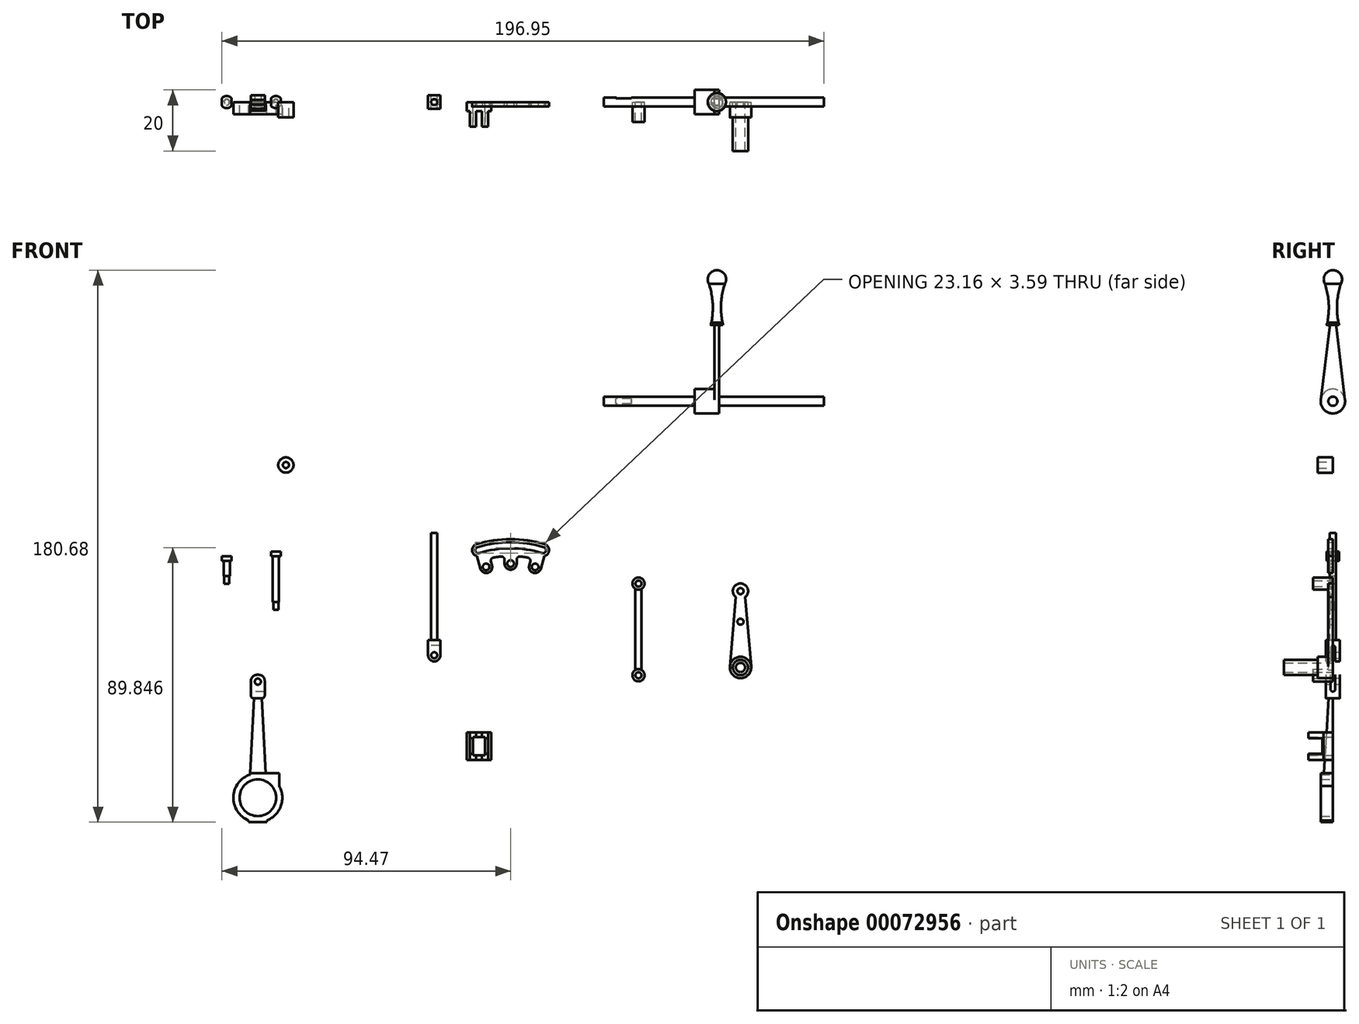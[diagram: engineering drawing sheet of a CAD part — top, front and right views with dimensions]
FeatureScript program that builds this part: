
annotation { "Feature Type Name" : "Feature", "Feature Type Description" : "" }
export const myFeature = defineFeature(function(context is Context, id is Id, definition is map)
    precondition{}
    {
        {
            var Q0;
            Q0=qCreatedBy(makeId("Front.planeOp"),FACE);
            var sketch = newSketch(context, id + "F0", { "sketchPlane" : qUnion([Q0])});
            skLineSegment(sketch, "E0", {"start": v(0, 0) * mm, "end": v(0, 28) * mm});
            skLineSegment(sketch, "E1", {"start": v(0, 0) * mm, "end": v(-7.48, 26.98) * mm});
            skCircle(sketch, "E2", {"center": v(0, 30) * mm, "radius": 1.1 * mm});
            skCircle(sketch, "E3", {"center": v(-8.02, 28.9) * mm, "radius": 1.1 * mm});
            skLineSegment(sketch, "E4", {"start": v(0, 0) * mm, "end": v(8.28, 26.93) * mm});
            skArc(sketch, "E5", {"start": v(11.08, 32.47) * mm, "mid": v(12.58, 34.36) * mm, "end": v(11.17, 36.32) * mm});
            skArc(sketch, "E6", {"start": v(10.3, 33.45) * mm, "mid": v(11.54, 34.11) * mm, "end": v(10.88, 35.36) * mm});
            skArc(sketch, "E7", {"start": v(-9.94, 28.37) * mm, "mid": v(-7.48, 26.98) * mm, "end": v(-6.09, 29.44) * mm});
            skLineSegment(sketch, "E8", {"start": v(-6.09, 29.44) * mm, "end": v(-6.44, 30.7) * mm});
            skLineSegment(sketch, "E9", {"start": v(-9.94, 28.37) * mm, "end": v(-10.73, 31.2) * mm});
            skArc(sketch, "E10.trimOffspring", {"start": v(9.93, 28.31) * mm, "mid": v(8.02, 28.9) * mm, "end": v(6.07, 29.38) * mm});
            skArc(sketch, "E11", {"start": v(10.3, 33.45) * mm, "mid": v(0, 35) * mm, "end": v(-10.3, 33.45) * mm});
            skArc(sketch, "E12", {"start": v(10.88, 35.36) * mm, "mid": v(0, 37) * mm, "end": v(-10.88, 35.36) * mm});
            skArc(sketch, "E13.MirrorC", {"start": v(-10.3, 33.45) * mm, "mid": v(-11.54, 34.11) * mm, "end": v(-10.88, 35.36) * mm});
            skArc(sketch, "E14.MirrorC", {"start": v(-11.08, 32.47) * mm, "mid": v(-12.58, 34.36) * mm, "end": v(-11.17, 36.32) * mm});
            skArc(sketch, "E15", {"start": v(11.17, 36.32) * mm, "mid": v(0, 38) * mm, "end": v(-11.17, 36.32) * mm});
            skLineSegment(sketch, "E16", {"start": v(-10.73, 31.2) * mm, "end": v(-11.08, 32.47) * mm});
            skLineSegment(sketch, "E17.MirrorCS", {"start": v(10.73, 31.2) * mm, "end": v(11.08, 32.47) * mm});
            skLineSegment(sketch, "E18.MirrorCS", {"start": v(9.94, 28.37) * mm, "end": v(10.73, 31.2) * mm});
            skLineSegment(sketch, "E19.MirrorCS", {"start": v(6.09, 29.44) * mm, "end": v(6.44, 30.7) * mm});
            skCircle(sketch, "E20.MirrorC", {"center": v(8.02, 28.9) * mm, "radius": 1.1 * mm});
            skArc(sketch, "E21.MirrorCS", {"start": v(9.94, 28.37) * mm, "mid": v(7.48, 26.98) * mm, "end": v(6.09, 29.44) * mm});
            skArc(sketch, "E22", {"start": v(-2, 30) * mm, "mid": v(0, 28) * mm, "end": v(2, 30) * mm});
            skLineSegment(sketch, "E23", {"start": v(0, 30) * mm, "end": v(2, 30) * mm});
            skLineSegment(sketch, "E24", {"start": v(2, 30) * mm, "end": v(2, 31.3) * mm});
            skLineSegment(sketch, "E25.MirrorCS", {"start": v(-2, 30) * mm, "end": v(-2, 31.3) * mm});
            skArc(sketch, "E26.trimOffspring", {"start": v(5.65, 31.95) * mm, "mid": v(4.38, 32.15) * mm, "end": v(3.1, 32.3) * mm});
            skArc(sketch, "E27.trimOffspring", {"start": v(-3.1, 32.3) * mm, "mid": v(-4.38, 32.15) * mm, "end": v(-5.65, 31.95) * mm});
            skPoint(sketch, "E28.trimOffspring.end.orphan", {"position": v(10, 32.5) * mm});
            skPoint(sketch, "E29.visualSharp", {"position": v(-6.73, 31.74) * mm});
            skArc(sketch, "E29.filletArc", {"start": v(-5.65, 31.95) * mm, "mid": v(-6.32, 31.5) * mm, "end": v(-6.44, 30.7) * mm});
            skPoint(sketch, "E30.visualSharp", {"position": v(-2, 32.39) * mm});
            skArc(sketch, "E30.filletArc", {"start": v(-2, 31.3) * mm, "mid": v(-2.33, 32.05) * mm, "end": v(-3.1, 32.3) * mm});
            skPoint(sketch, "E31.visualSharp", {"position": v(2, 32.39) * mm});
            skArc(sketch, "E31.filletArc", {"start": v(3.1, 32.3) * mm, "mid": v(2.33, 32.05) * mm, "end": v(2, 31.3) * mm});
            skPoint(sketch, "E32.visualSharp", {"position": v(6.73, 31.74) * mm});
            skArc(sketch, "E32.filletArc", {"start": v(6.44, 30.7) * mm, "mid": v(6.32, 31.5) * mm, "end": v(5.65, 31.95) * mm});
            skSolve(sketch);
        }
        {
            var Q0;
            Q0=makeQuery(id+"F0.imprint","IMPRINT",FACE,{"disambiguationData":[TD([[makeQuery(id+"F0.imprint","IMPRINT",EDGE,{"derivedFrom":sQuery(id+"F0.wireOp",EDGE,"E2")}),-1.0]])]});
            var Q1;
            {var subQ0=sQuery(id+"F0.wireOp",EDGE,"E21.MirrorCS");var subQ1=sQuery(id+"F0.wireOp",EDGE,"E10.trimOffspring");var subQ7=makeQuery(id+"F0.imprint","INTERSECT",VERTEX,{"disambiguationData":[OD(0.0)],"derivedFrom":[subQ1,subQ0]});Q1=makeQuery(id+"F0.imprint","IMPRINT",FACE,{"disambiguationData":[TD([[makeQuery(id+"F0.imprint","IMPRINT",EDGE,{"disambiguationData":[TD([[subQ7,-1.0]])],"derivedFrom":subQ1}),1.0]])]});}
            extrude(context, id + "F1", {"entities" : qUnion([Q0, Q1]), "depth" : 1.5 * mm});
        }
        {
            var Q0;
            Q0=qCreatedBy(makeId("Front.planeOp"),FACE);
            var sketch = newSketch(context, id + "F2", { "sketchPlane" : qUnion([Q0])});
            skLineSegment(sketch, "E33", {"start": v(0, 0) * mm, "end": v(-25, 0) * mm});
            skCircle(sketch, "E34", {"center": v(-25, 0) * mm, "radius": 1 * mm});
            skArc(sketch, "E35", {"start": v(-27, 0) * mm, "mid": v(-25, -2) * mm, "end": v(-23, 0) * mm});
            skLineSegment(sketch, "E36", {"start": v(-27, 0) * mm, "end": v(-27, 5) * mm});
            skLineSegment(sketch, "E37", {"start": v(-25, 0) * mm, "end": v(-25, -0.62) * mm});
            skLineSegment(sketch, "E38.MirrorCS", {"start": v(-23, 0) * mm, "end": v(-23, 5) * mm});
            skLineSegment(sketch, "E39", {"start": v(-27, 5) * mm, "end": v(-23, 5) * mm});
            skSolve(sketch);
        }
        {
            var Q0;
            Q0 = qSketchRegion(id + "F2", true);
            extrude(context, id + "F3", {"entities" : qUnion([Q0]), "endBound" : BoundingType.SYMMETRIC, "depth" : 4.5 * mm});
        }
        {
            var Q0;
            Q0=makeQuery(id+"F3.opExtrude","SWEPT_FACE",FACE,{"disambiguationData":[OSD([sQuery(id+"F2.wireOp",EDGE,"E36")])]});
            var sketch = newSketch(context, id + "F4", { "sketchPlane" : qUnion([Q0])});
            skLineSegment(sketch, "E40", {"start": v(0, 0) * mm, "end": v(0, 2.5) * mm});
            skPoint(sketch, "E40.endSnap0", {"position": v(0, 0) * mm});
            skArc(sketch, "E41", {"start": v(0.75, 2.5) * mm, "mid": v(0, 3.25) * mm, "end": v(-0.75, 2.5) * mm});
            skLineSegment(sketch, "E42", {"start": v(-0.75, 2.5) * mm, "end": v(-0.75, -3.17) * mm});
            skLineSegment(sketch, "E43", {"start": v(-0.75, -3.17) * mm, "end": v(0, -3.17) * mm});
            skLineSegment(sketch, "E44", {"start": v(0, -3.17) * mm, "end": v(1.6, -3.17) * mm});
            skLineSegment(sketch, "E45", {"start": v(0.75, 2.5) * mm, "end": v(0.75, -3.17) * mm});
            skSolve(sketch);
        }
        {
            var Q0;
            Q0 = qSketchRegion(id + "F4", true);
            extrude(context, id + "F5", {"entities" : qUnion([Q0]), "operationType" : NewBodyOperationType.REMOVE, "endBound" : BoundingType.SYMMETRIC, "oppositeDirection" : true, "depth" : 25 * mm});
        }
        {
            var Q0;
            Q0=makeQuery(id+"F3.opExtrude","SWEPT_FACE",FACE,{"disambiguationData":[OSD([sQuery(id+"F2.wireOp",EDGE,"E39")])]});
            var sketch = newSketch(context, id + "F6", { "sketchPlane" : qUnion([Q0])});
            skCircle(sketch, "E46", {"center": v(-25, 0) * mm, "radius": 1 * mm});
            skPoint(sketch, "E46.centerSnap0", {"position": v(-25, 2.25) * mm});
            skPoint(sketch, "E46.centerSnap1", {"position": v(-27, 0) * mm});
            skSolve(sketch);
        }
        {
            var Q0;
            Q0 = qSketchRegion(id + "F6", true);
            extrude(context, id + "F7", {"entities" : qUnion([Q0]), "operationType" : NewBodyOperationType.ADD, "depth" : 35 * mm});
        }
        {
            var Q0;
            Q0=qCreatedBy(makeId("Front.planeOp"),FACE);
            var sketch = newSketch(context, id + "F8", { "sketchPlane" : qUnion([Q0])});
            skCircle(sketch, "E47", {"center": v(41.83, 23.44) * mm, "radius": 1 * mm});
            skCircle(sketch, "E48", {"center": v(41.83, 23.44) * mm, "radius": 2 * mm});
            skCircle(sketch, "E49", {"center": v(41.83, -6.56) * mm, "radius": 1 * mm});
            skCircle(sketch, "E50", {"center": v(41.83, -6.56) * mm, "radius": 2 * mm});
            skLineSegment(sketch, "E51", {"start": v(41.83, 23.44) * mm, "end": v(40.83, 23.44) * mm});
            skLineSegment(sketch, "E52", {"start": v(40.83, 21.7) * mm, "end": v(40.83, -4.83) * mm});
            skLineSegment(sketch, "E53.MirrorCS", {"start": v(42.83, 21.7) * mm, "end": v(42.83, -4.83) * mm});
            skSolve(sketch);
        }
        {
            var Q0;
            {var subQ0=sQuery(id+"F8.wireOp",EDGE,"E52");Q0=makeQuery(id+"F8.imprint","IMPRINT",FACE,{"disambiguationData":[TD([[makeQuery(id+"F8.imprint","IMPRINT",EDGE,{"derivedFrom":subQ0}),1.0]])]});}
            extrude(context, id + "F9", {"entities" : qUnion([Q0]), "depth" : 1.5 * mm});
        }
        {
            var Q0;
            Q0=makeQuery(id+"F8.imprint","IMPRINT",FACE,{"disambiguationData":[TD([[makeQuery(id+"F8.imprint","IMPRINT",EDGE,{"derivedFrom":sQuery(id+"F8.wireOp",EDGE,"E49")}),-1.0]])]});
            var Q1;
            Q1=makeQuery(id+"F8.imprint","IMPRINT",FACE,{"disambiguationData":[TD([[makeQuery(id+"F8.imprint","IMPRINT",EDGE,{"derivedFrom":sQuery(id+"F8.wireOp",EDGE,"E47")}),-1.0]])]});
            extrude(context, id + "F10", {"entities" : qUnion([Q0, Q1]), "operationType" : NewBodyOperationType.ADD, "depth" : 6.5 * mm});
        }
        {
            var Q0;
            Q0=qCreatedBy(makeId("Front.planeOp"),FACE);
            var sketch = newSketch(context, id + "F11", { "sketchPlane" : qUnion([Q0])});
            skLineSegment(sketch, "E54", {"start": v(75.2, -4.01) * mm, "end": v(75.2, 20.99) * mm});
            skCircle(sketch, "E55", {"center": v(75.2, 20.99) * mm, "radius": 1 * mm});
            skCircle(sketch, "E56", {"center": v(75.2, 20.99) * mm, "radius": 2.5 * mm});
            skCircle(sketch, "E57", {"center": v(75.2, -4.01) * mm, "radius": 2.5 * mm});
            skCircle(sketch, "E58", {"center": v(75.2, -4.01) * mm, "radius": 3.5 * mm});
            skCircle(sketch, "E59", {"center": v(75.2, -4.01) * mm, "radius": 1.5 * mm});
            skLineSegment(sketch, "E60", {"start": v(76.74, 19.02) * mm, "end": v(78.68, -3.71) * mm});
            skLineSegment(sketch, "E61.MirrorCS", {"start": v(73.65, 19.02) * mm, "end": v(71.7, -3.71) * mm});
            skLineSegment(sketch, "E62", {"start": v(75.2, 20.99) * mm, "end": v(75.2, 10.99) * mm});
            skCircle(sketch, "E63", {"center": v(75.2, 10.99) * mm, "radius": 1 * mm});
            skSolve(sketch);
        }
        {
            var Q0;
            {var subQ0=sQuery(id+"F11.wireOp",EDGE,"E60");Q0=makeQuery(id+"F11.imprint","IMPRINT",FACE,{"disambiguationData":[TD([[makeQuery(id+"F11.imprint","IMPRINT",EDGE,{"derivedFrom":subQ0}),-1.0]])]});}
            var Q1;
            {var subQ0=sQuery(id+"F11.wireOp",EDGE,"E61.MirrorCS");Q1=makeQuery(id+"F11.imprint","IMPRINT",FACE,{"disambiguationData":[TD([[makeQuery(id+"F11.imprint","IMPRINT",EDGE,{"derivedFrom":subQ0}),1.0]])]});}
            var Q2;
            Q2=makeQuery(id+"F11.imprint","IMPRINT",FACE,{"disambiguationData":[TD([[makeQuery(id+"F11.imprint","IMPRINT",EDGE,{"derivedFrom":sQuery(id+"F11.wireOp",EDGE,"E55")}),-1.0]])]});
            extrude(context, id + "F12", {"entities" : qUnion([Q0, Q1, Q2]), "depth" : 1.5 * mm});
        }
        {
            var Q0;
            Q0=makeQuery(id+"F11.imprint","IMPRINT",FACE,{"disambiguationData":[TD([[makeQuery(id+"F11.imprint","IMPRINT",EDGE,{"derivedFrom":sQuery(id+"F11.wireOp",EDGE,"E57")}),-1.0]])]});
            extrude(context, id + "F13", {"entities" : qUnion([Q0]), "operationType" : NewBodyOperationType.ADD, "depth" : 5 * mm});
        }
        {
            var Q0;
            Q0=makeQuery(id+"F11.imprint","IMPRINT",FACE,{"disambiguationData":[TD([[makeQuery(id+"F11.imprint","IMPRINT",EDGE,{"derivedFrom":sQuery(id+"F11.wireOp",EDGE,"E57")}),1.0]])]});
            extrude(context, id + "F14", {"entities" : qUnion([Q0]), "operationType" : NewBodyOperationType.ADD, "depth" : 16 * mm});
        }
        {
            var Q0;
            Q0=qCreatedBy(makeId("Front.planeOp"),FACE);
            var sketch = newSketch(context, id + "F15", { "sketchPlane" : qUnion([Q0])});
            skLineSegment(sketch, "E64.left", {"start": v(-14.34, -25.22) * mm, "end": v(-14.34, -29.72) * mm});
            skLineSegment(sketch, "E65", {"start": v(-14.34, -25.22) * mm, "end": v(-10.34, -25.22) * mm});
            skLineSegment(sketch, "E66", {"start": v(-10.34, -25.22) * mm, "end": v(-10.34, -26.72) * mm});
            skLineSegment(sketch, "E67.MirrorCS", {"start": v(-6.34, -25.22) * mm, "end": v(-10.34, -25.22) * mm});
            skLineSegment(sketch, "E68", {"start": v(-14.34, -29.72) * mm, "end": v(-15.04, -29.72) * mm});
            skLineSegment(sketch, "E69.MirrorCS", {"start": v(-14.34, -34.22) * mm, "end": v(-14.34, -29.72) * mm});
            skLineSegment(sketch, "E70", {"start": v(-10.34, -26.72) * mm, "end": v(-12.34, -26.72) * mm});
            skLineSegment(sketch, "E71.MirrorCS", {"start": v(-10.34, -32.72) * mm, "end": v(-12.34, -32.72) * mm});
            skLineSegment(sketch, "E72.MirrorCS", {"start": v(-10.34, -26.72) * mm, "end": v(-8.34, -26.72) * mm});
            skLineSegment(sketch, "E73.MirrorCS", {"start": v(-10.34, -32.72) * mm, "end": v(-8.34, -32.72) * mm});
            skLineSegment(sketch, "E74", {"start": v(-12.34, -26.72) * mm, "end": v(-12.34, -32.72) * mm});
            skLineSegment(sketch, "E75", {"start": v(-8.34, -26.72) * mm, "end": v(-8.34, -32.87) * mm});
            skLineSegment(sketch, "E76.MirrorCS", {"start": v(-6.34, -25.22) * mm, "end": v(-6.34, -29.72) * mm});
            skLineSegment(sketch, "E77.MirrorCS", {"start": v(-6.34, -34.22) * mm, "end": v(-6.34, -29.72) * mm});
            skLineSegment(sketch, "E78.MirrorCS", {"start": v(-14.34, -34.22) * mm, "end": v(-10.34, -34.22) * mm});
            skLineSegment(sketch, "E79.MirrorCS", {"start": v(-6.34, -34.22) * mm, "end": v(-10.34, -34.22) * mm});
            skSolve(sketch);
        }
        {
            var Q0;
            Q0 = qSketchRegion(id + "F15", true);
            extrude(context, id + "F16", {"entities" : qUnion([Q0]), "depth" : 8 * mm});
        }
        {
            var Q0;
            Q0=makeQuery(id+"F16.opExtrude","SWEPT_FACE",FACE,{"disambiguationData":[OSD([sQuery(id+"F15.wireOp",EDGE,"E76.MirrorCS"),sQuery(id+"F15.wireOp",EDGE,"E77.MirrorCS")])]});
            var sketch = newSketch(context, id + "F17", { "sketchPlane" : qUnion([Q0])});
            skLineSegment(sketch, "E80", {"start": v(0, -29.72) * mm, "end": v(0, -27.22) * mm});
            skLineSegment(sketch, "E81", {"start": v(0, -27.22) * mm, "end": v(-3.5, -27.22) * mm});
            skLineSegment(sketch, "E82", {"start": v(-3.5, -27.22) * mm, "end": v(-3.5, -29.72) * mm});
            skLineSegment(sketch, "E83", {"start": v(0, -29.72) * mm, "end": v(2.8, -29.72) * mm});
            skLineSegment(sketch, "E84.MirrorCS", {"start": v(-3.5, -32.22) * mm, "end": v(-3.5, -29.72) * mm});
            skLineSegment(sketch, "E85.MirrorCS", {"start": v(0, -32.22) * mm, "end": v(-3.5, -32.22) * mm});
            skLineSegment(sketch, "E86", {"start": v(-3.5, -32.22) * mm, "end": v(-8, -32.22) * mm});
            skLineSegment(sketch, "E87", {"start": v(-8, -32.22) * mm, "end": v(-8, -34.22) * mm});
            skLineSegment(sketch, "E88", {"start": v(-8, -34.22) * mm, "end": v(0, -34.22) * mm});
            skLineSegment(sketch, "E89", {"start": v(0, -34.22) * mm, "end": v(0, -32.22) * mm});
            skLineSegment(sketch, "E90.MirrorCS", {"start": v(-3.5, -27.22) * mm, "end": v(-8, -27.22) * mm});
            skLineSegment(sketch, "E91.MirrorCS", {"start": v(-8, -27.22) * mm, "end": v(-8, -25.22) * mm});
            skLineSegment(sketch, "E92.MirrorCS", {"start": v(-8, -25.22) * mm, "end": v(0, -25.22) * mm});
            skLineSegment(sketch, "E93.MirrorCS", {"start": v(0, -25.22) * mm, "end": v(0, -27.22) * mm});
            skLineSegment(sketch, "E94", {"start": v(-8, -32.22) * mm, "end": v(-8, -27.22) * mm});
            skSolve(sketch);
        }
        {
            var Q0;
            Q0=makeQuery(id+"F17.imprint","IMPRINT",FACE,{"disambiguationData":[TD([[makeQuery(id+"F17.imprint","IMPRINT",EDGE,{"derivedFrom":sQuery(id+"F17.wireOp",EDGE,"E82")}),-1.0]])]});
            extrude(context, id + "F18", {"entities" : qUnion([Q0]), "operationType" : NewBodyOperationType.REMOVE, "oppositeDirection" : true, "depth" : 25 * mm});
        }
        {
            var Q0;
            Q0=makeQuery(id+"F16.opExtrude","SWEPT_FACE",FACE,{"disambiguationData":[OSD([sQuery(id+"F15.wireOp",EDGE,"E78.MirrorCS"),sQuery(id+"F15.wireOp",EDGE,"E79.MirrorCS")])]});
            var sketch = newSketch(context, id + "F19", { "sketchPlane" : qUnion([Q0])});
            skLineSegment(sketch, "E95", {"start": v(-14.34, 0) * mm, "end": v(-14.34, 3) * mm});
            skLineSegment(sketch, "E96", {"start": v(-10.34, 0) * mm, "end": v(-10.34, 8) * mm});
            skLineSegment(sketch, "E97", {"start": v(-10.34, 8) * mm, "end": v(-11.34, 8) * mm});
            skLineSegment(sketch, "E98", {"start": v(-11.34, 8) * mm, "end": v(-13.34, 8) * mm});
            skLineSegment(sketch, "E99", {"start": v(-14.34, 3) * mm, "end": v(-13.34, 3) * mm});
            skLineSegment(sketch, "E100", {"start": v(-13.34, 3) * mm, "end": v(-13.34, 8) * mm});
            skLineSegment(sketch, "E101", {"start": v(-13.34, 8) * mm, "end": v(-11.34, 8) * mm});
            skLineSegment(sketch, "E102", {"start": v(-11.34, 8) * mm, "end": v(-11.34, 3) * mm});
            skLineSegment(sketch, "E103", {"start": v(-11.34, 3) * mm, "end": v(-10.34, 3) * mm});
            skLineSegment(sketch, "E104.MirrorCS", {"start": v(-9.34, 3) * mm, "end": v(-10.34, 3) * mm});
            skLineSegment(sketch, "E105.MirrorCS", {"start": v(-9.34, 8) * mm, "end": v(-9.34, 3) * mm});
            skLineSegment(sketch, "E106.MirrorCS", {"start": v(-7.34, 8) * mm, "end": v(-9.34, 8) * mm});
            skLineSegment(sketch, "E107.MirrorCS", {"start": v(-7.34, 3) * mm, "end": v(-7.34, 8) * mm});
            skLineSegment(sketch, "E108.MirrorCS", {"start": v(-6.34, 3) * mm, "end": v(-7.34, 3) * mm});
            skLineSegment(sketch, "E109.MirrorCS", {"start": v(-6.34, 0) * mm, "end": v(-6.34, 3) * mm});
            skLineSegment(sketch, "E110.bottom", {"start": v(-14.34, 3) * mm, "end": v(-6.34, 3) * mm});
            skLineSegment(sketch, "E110.top", {"start": v(-14.34, 8) * mm, "end": v(-6.34, 8) * mm});
            skLineSegment(sketch, "E110.left", {"start": v(-14.34, 3) * mm, "end": v(-14.34, 8) * mm});
            skLineSegment(sketch, "E110.right", {"start": v(-6.34, 3) * mm, "end": v(-6.34, 8) * mm});
            skSolve(sketch);
        }
        {
            var Q0;
            {var subQ0=sQuery(id+"F19.wireOp",EDGE,"E100");Q0=makeQuery(id+"F19.imprint","IMPRINT",FACE,{"disambiguationData":[TD([[makeQuery(id+"F19.imprint","IMPRINT",EDGE,{"derivedFrom":subQ0}),1.0]])]});}
            var Q1;
            {var subQ5=sQuery(id+"F19.wireOp",EDGE,"E102");Q1=makeQuery(id+"F19.imprint","IMPRINT",FACE,{"disambiguationData":[TD([[makeQuery(id+"F19.imprint","IMPRINT",EDGE,{"derivedFrom":subQ5}),1.0]])]});}
            var Q2;
            {var subQ5=sQuery(id+"F19.wireOp",EDGE,"E105.MirrorCS");Q2=makeQuery(id+"F19.imprint","IMPRINT",FACE,{"disambiguationData":[TD([[makeQuery(id+"F19.imprint","IMPRINT",EDGE,{"derivedFrom":subQ5}),-1.0]])]});}
            var Q3;
            {var subQ0=sQuery(id+"F19.wireOp",EDGE,"E107.MirrorCS");Q3=makeQuery(id+"F19.imprint","IMPRINT",FACE,{"disambiguationData":[TD([[makeQuery(id+"F19.imprint","IMPRINT",EDGE,{"derivedFrom":subQ0}),-1.0]])]});}
            extrude(context, id + "F20", {"entities" : qUnion([Q0, Q1, Q2, Q3]), "operationType" : NewBodyOperationType.REMOVE, "oppositeDirection" : true, "depth" : 25 * mm});
        }
        {
            var Q0;
            Q0=qCreatedBy(makeId("Front.planeOp"),FACE);
            var sketch = newSketch(context, id + "F21", { "sketchPlane" : qUnion([Q0])});
            skCircle(sketch, "E111", {"center": v(-82.7, -46.64) * mm, "radius": 8 * mm});
            skCircle(sketch, "E112", {"center": v(-82.7, -46.64) * mm, "radius": 6 * mm});
            skLineSegment(sketch, "E113", {"start": v(-82.7, -46.64) * mm, "end": v(-82.7, -14.14) * mm});
            skLineSegment(sketch, "E114", {"start": v(-82.7, -14.14) * mm, "end": v(-82.7, -19.64) * mm});
            skLineSegment(sketch, "E115", {"start": v(-82.7, -38.64) * mm, "end": v(-80.2, -38.64) * mm});
            skLineSegment(sketch, "E116", {"start": v(-80.2, -38.64) * mm, "end": v(-80.2, -39.04) * mm});
            skLineSegment(sketch, "E117.MirrorCS", {"start": v(-82.7, -38.64) * mm, "end": v(-85.2, -38.64) * mm});
            skLineSegment(sketch, "E118.MirrorCS", {"start": v(-85.2, -38.64) * mm, "end": v(-85.2, -39.04) * mm});
            skLineSegment(sketch, "E119", {"start": v(-82.7, -14.14) * mm, "end": v(-83.95, -14.14) * mm});
            skLineSegment(sketch, "E120", {"start": v(-83.95, -14.14) * mm, "end": v(-85.2, -38.64) * mm});
            skLineSegment(sketch, "E121.MirrorCS", {"start": v(-81.45, -14.14) * mm, "end": v(-80.2, -38.64) * mm});
            skLineSegment(sketch, "E122", {"start": v(-82.7, -46.64) * mm, "end": v(-82.7, -54.64) * mm});
            skLineSegment(sketch, "E123", {"start": v(-82.7, -54.64) * mm, "end": v(-79.7, -54.64) * mm});
            skLineSegment(sketch, "E124", {"start": v(-79.7, -54.64) * mm, "end": v(-79.7, -54.05) * mm});
            skLineSegment(sketch, "E125.MirrorCS", {"start": v(-82.7, -54.64) * mm, "end": v(-85.7, -54.64) * mm});
            skLineSegment(sketch, "E126.MirrorCS", {"start": v(-85.7, -54.64) * mm, "end": v(-85.7, -54.05) * mm});
            skLineSegment(sketch, "E127", {"start": v(-82.7, -38.64) * mm, "end": v(-75.7, -38.64) * mm});
            skLineSegment(sketch, "E128", {"start": v(-75.7, -38.64) * mm, "end": v(-75.7, -42.77) * mm});
            skLineSegment(sketch, "E129", {"start": v(-81.45, -14.14) * mm, "end": v(-82.7, -14.14) * mm});
            skSolve(sketch);
        }
        {
            var Q0;
            Q0 = qSketchRegion(id + "F21", true);
            extrude(context, id + "F22", {"entities" : qUnion([Q0]), "depth" : 4 * mm});
        }
        {
            var Q0;
            Q0=makeQuery(id+"F22.opExtrude","SWEPT_FACE",FACE,{"disambiguationData":[OSD([sQuery(id+"F21.wireOp",EDGE,"E126.MirrorCS")])]});
            var sketch = newSketch(context, id + "F23", { "sketchPlane" : qUnion([Q0])});
            skLineSegment(sketch, "E130", {"start": v(0, -54.64) * mm, "end": v(0, -14.14) * mm});
            skLineSegment(sketch, "E131", {"start": v(0, -14.14) * mm, "end": v(1.4, -14.14) * mm});
            skLineSegment(sketch, "E132", {"start": v(0, -54.64) * mm, "end": v(0, -38.64) * mm});
            skLineSegment(sketch, "E133", {"start": v(0, -38.64) * mm, "end": v(2.9, -38.64) * mm});
            skLineSegment(sketch, "E134", {"start": v(2.9, -38.64) * mm, "end": v(1.4, -14.14) * mm});
            skLineSegment(sketch, "E135", {"start": v(1.4, -14.14) * mm, "end": v(5.38, -14.14) * mm});
            skLineSegment(sketch, "E136", {"start": v(5.38, -14.14) * mm, "end": v(5.38, -38.64) * mm});
            skLineSegment(sketch, "E137", {"start": v(5.38, -38.64) * mm, "end": v(2.9, -38.64) * mm});
            skSolve(sketch);
        }
        {
            var Q0;
            Q0=makeQuery(id+"F23.imprint","IMPRINT",FACE,{"disambiguationData":[TD([[makeQuery(id+"F23.imprint","IMPRINT",EDGE,{"derivedFrom":sQuery(id+"F23.wireOp",EDGE,"E134")}),-1.0]])]});
            extrude(context, id + "F24", {"entities" : qUnion([Q0]), "operationType" : NewBodyOperationType.REMOVE, "oppositeDirection" : true, "depth" : 25 * mm});
        }
        {
            var Q0;
            Q0=makeQuery(id+"F22.opExtrude","CAP_FACE",FACE,{"disambiguationData":[OSD([sQuery(id+"F21.wireOp",EDGE,"E111"),sQuery(id+"F21.wireOp",EDGE,"E112"),sQuery(id+"F21.wireOp",EDGE,"E118.MirrorCS"),sQuery(id+"F21.wireOp",EDGE,"E119"),sQuery(id+"F21.wireOp",EDGE,"E120"),sQuery(id+"F21.wireOp",EDGE,"E121.MirrorCS"),sQuery(id+"F21.wireOp",EDGE,"E123"),sQuery(id+"F21.wireOp",EDGE,"E124"),sQuery(id+"F21.wireOp",EDGE,"E125.MirrorCS"),sQuery(id+"F21.wireOp",EDGE,"E126.MirrorCS"),sQuery(id+"F21.wireOp",EDGE,"E127"),sQuery(id+"F21.wireOp",EDGE,"E128"),sQuery(id+"F21.wireOp",EDGE,"E129")])],"isStart":true});
            var sketch = newSketch(context, id + "F25", { "sketchPlane" : qUnion([Q0])});
            skLineSegment(sketch, "E138", {"start": v(82.7, -14.14) * mm, "end": v(82.7, -8.64) * mm});
            skCircle(sketch, "E139", {"center": v(82.7, -8.64) * mm, "radius": 1 * mm});
            skLineSegment(sketch, "E140.MirrorCS", {"start": v(84.95, -6.4) * mm, "end": v(84.95, -4.15) * mm});
            skLineSegment(sketch, "E141", {"start": v(82.7, -8.64) * mm, "end": v(82.7, -6.39) * mm});
            skLineSegment(sketch, "E142", {"start": v(82.7, -6.39) * mm, "end": v(82.95, -6.39) * mm});
            skLineSegment(sketch, "E143", {"start": v(84.95, -8.39) * mm, "end": v(84.95, -8.64) * mm});
            skLineSegment(sketch, "E144.MirrorCS", {"start": v(82.7, -6.39) * mm, "end": v(82.44, -6.39) * mm});
            skLineSegment(sketch, "E145.MirrorCS", {"start": v(80.45, -8.39) * mm, "end": v(80.45, -8.64) * mm});
            skPoint(sketch, "E146.visualSharp", {"position": v(84.95, -6.4) * mm});
            skArc(sketch, "E146.filletArc", {"start": v(84.95, -8.39) * mm, "mid": v(84.36, -6.98) * mm, "end": v(82.95, -6.39) * mm});
            skPoint(sketch, "E147.visualSharp", {"position": v(80.45, -6.4) * mm});
            skArc(sketch, "E147.filletArc", {"start": v(82.44, -6.39) * mm, "mid": v(81.03, -6.98) * mm, "end": v(80.45, -8.39) * mm});
            skLineSegment(sketch, "E148", {"start": v(80.45, -8.64) * mm, "end": v(80.45, -13.14) * mm});
            skLineSegment(sketch, "E149", {"start": v(81.45, -14.14) * mm, "end": v(82.7, -14.14) * mm});
            skPoint(sketch, "E150.visualSharp", {"position": v(80.45, -14.14) * mm});
            skArc(sketch, "E150.filletArc", {"start": v(80.45, -13.14) * mm, "mid": v(80.74, -13.85) * mm, "end": v(81.45, -14.14) * mm});
            skLineSegment(sketch, "E151.MirrorCS", {"start": v(84.95, -8.64) * mm, "end": v(84.95, -13.14) * mm});
            skArc(sketch, "E152.MirrorCS", {"start": v(84.95, -13.14) * mm, "mid": v(84.65, -13.85) * mm, "end": v(83.95, -14.14) * mm});
            skLineSegment(sketch, "E153.MirrorCS", {"start": v(83.95, -14.14) * mm, "end": v(82.7, -14.14) * mm});
            skSolve(sketch);
        }
        {
            var Q0;
            Q0 = qSketchRegion(id + "F25", true);
            extrude(context, id + "F26", {"entities" : qUnion([Q0]), "operationType" : NewBodyOperationType.ADD, "depth" : 2.25 * mm, "hasSecondDirection" : true, "secondDirectionOppositeDirection" : true, "secondDirectionDepth" : 2.25 * mm});
        }
        {
            var Q0;
            Q0=makeQuery(id+"F26.opExtrude","SWEPT_FACE",FACE,{"disambiguationData":[OSD([sQuery(id+"F25.wireOp",EDGE,"E143"),sQuery(id+"F25.wireOp",EDGE,"E151.MirrorCS")])]});
            var sketch = newSketch(context, id + "F27", { "sketchPlane" : qUnion([Q0])});
            skLineSegment(sketch, "E154", {"start": v(0, -13.14) * mm, "end": v(0, -14.14) * mm});
            skLineSegment(sketch, "E155", {"start": v(0, -14.14) * mm, "end": v(0, -8.64) * mm});
            skLineSegment(sketch, "E156", {"start": v(0, -8.64) * mm, "end": v(0, -11.14) * mm});
            skCircle(sketch, "E157", {"center": v(0, -11.14) * mm, "radius": 0.75 * mm});
            skLineSegment(sketch, "E158", {"start": v(0, -11.14) * mm, "end": v(0.75, -11.14) * mm});
            skLineSegment(sketch, "E159", {"start": v(0.75, -11.14) * mm, "end": v(0.75, -6.2) * mm});
            skLineSegment(sketch, "E160", {"start": v(0.75, -6.2) * mm, "end": v(-0.75, -6.2) * mm});
            skLineSegment(sketch, "E161", {"start": v(-0.75, -6.2) * mm, "end": v(-0.75, -11.14) * mm});
            skSolve(sketch);
        }
        {
            var Q0;
            Q0 = qSketchRegion(id + "F27", true);
            extrude(context, id + "F28", {"entities" : qUnion([Q0]), "operationType" : NewBodyOperationType.REMOVE, "oppositeDirection" : true, "depth" : 25 * mm});
        }
        {
            var Q0;
            Q0=qCreatedBy(makeId("Front.planeOp"),FACE);
            var sketch = newSketch(context, id + "F29", { "sketchPlane" : qUnion([Q0])});
            skLineSegment(sketch, "E162", {"start": v(-92.87, 23.43) * mm, "end": v(-92.87, 25.93) * mm});
            skLineSegment(sketch, "E163", {"start": v(-92.87, 25.93) * mm, "end": v(-91.87, 25.93) * mm});
            skLineSegment(sketch, "E164", {"start": v(-92.87, 25.93) * mm, "end": v(-92.87, 30.93) * mm});
            skLineSegment(sketch, "E165", {"start": v(-92.87, 30.93) * mm, "end": v(-91.87, 30.93) * mm});
            skLineSegment(sketch, "E166", {"start": v(-91.87, 30.93) * mm, "end": v(-91.87, 25.93) * mm});
            skLineSegment(sketch, "E167", {"start": v(-92.87, 23.43) * mm, "end": v(-92.07, 23.43) * mm});
            skLineSegment(sketch, "E168", {"start": v(-92.07, 23.43) * mm, "end": v(-92.07, 25.93) * mm});
            skSolve(sketch);
        }
        {
            var Q0;
            Q0 = qSketchRegion(id + "F29", true);
            var Q1;
            Q1=sQuery(id+"F29.wireOp",EDGE,"E164");
            revolve(context, id + "F30", {"entities" : qUnion([Q0]), "axis" : qUnion([Q1]), "revolveType" : RevolveType.FULL});
        }
        {
            var Q0;
            Q0=makeQuery(id+"F30.opRevolve","SWEPT_FACE",FACE,{"disambiguationData":[OSD([sQuery(id+"F29.wireOp",EDGE,"E165")])]});
            var sketch = newSketch(context, id + "F31", { "sketchPlane" : qUnion([Q0])});
            skCircle(sketch, "E169", {"center": v(-92.87, 0) * mm, "radius": 2 * mm});
            skLineSegment(sketch, "E170", {"start": v(-92.87, 0) * mm, "end": v(-91.27, 0) * mm});
            skLineSegment(sketch, "E171", {"start": v(-91.27, 0) * mm, "end": v(-91.27, -1.2) * mm});
            skLineSegment(sketch, "E172", {"start": v(-91.27, -1.2) * mm, "end": v(-91.27, 1.2) * mm});
            skLineSegment(sketch, "E173", {"start": v(-92.87, 0) * mm, "end": v(-92.87, -0.42) * mm});
            skLineSegment(sketch, "E174.MirrorCS", {"start": v(-94.47, -1.2) * mm, "end": v(-94.47, 1.2) * mm});
            skSolve(sketch);
        }
        {
            var Q0;
            {var subQ5=sQuery(id+"F31.wireOp",EDGE,"E174.MirrorCS");Q0=makeQuery(id+"F31.imprint","IMPRINT",FACE,{"disambiguationData":[TD([[makeQuery(id+"F31.imprint","IMPRINT",EDGE,{"derivedFrom":subQ5}),-1.0]])]});}
            var Q1;
            Q1=makeQuery(id+"F31.imprint","IMPRINT",FACE,{"disambiguationData":[TD([[makeQuery(id+"F31.imprint","IMPRINT",EDGE,{"derivedFrom":makeQuery(id+"F30.opRevolve","SWEPT_EDGE",EDGE,{"disambiguationData":[OSD([sQuery(id+"F29.wireOp",EDGE,"E165"),sQuery(id+"F29.wireOp",EDGE,"E166")])]})}),-1.0]])]});
            extrude(context, id + "F32", {"entities" : qUnion([Q0, Q1]), "operationType" : NewBodyOperationType.ADD, "depth" : 1.5 * mm});
        }
        {
            var Q0;
            Q0=qCreatedBy(makeId("Front.planeOp"),FACE);
            var sketch = newSketch(context, id + "F33", { "sketchPlane" : qUnion([Q0])});
            skLineSegment(sketch, "E175", {"start": v(-76.8, 32.38) * mm, "end": v(-76.8, 17.38) * mm});
            skLineSegment(sketch, "E176", {"start": v(-76.8, 17.38) * mm, "end": v(-76.8, 14.88) * mm});
            skLineSegment(sketch, "E177", {"start": v(-76.8, 14.88) * mm, "end": v(-76, 14.88) * mm});
            skLineSegment(sketch, "E178", {"start": v(-76, 14.88) * mm, "end": v(-76, 17.38) * mm});
            skLineSegment(sketch, "E179", {"start": v(-76, 17.38) * mm, "end": v(-76.8, 17.38) * mm});
            skLineSegment(sketch, "E180", {"start": v(-76.8, 17.38) * mm, "end": v(-75.8, 17.38) * mm});
            skLineSegment(sketch, "E181", {"start": v(-75.8, 17.38) * mm, "end": v(-75.8, 32.38) * mm});
            skLineSegment(sketch, "E182", {"start": v(-75.8, 32.38) * mm, "end": v(-76.8, 32.38) * mm});
            skSolve(sketch);
        }
        {
            var Q0;
            Q0 = qSketchRegion(id + "F33", true);
            var Q1;
            Q1=sQuery(id+"F33.wireOp",EDGE,"E175");
            revolve(context, id + "F34", {"entities" : qUnion([Q0]), "axis" : qUnion([Q1]), "revolveType" : RevolveType.FULL});
        }
        {
            var Q0;
            Q0=makeQuery(id+"F34.opRevolve","SWEPT_FACE",FACE,{"disambiguationData":[OSD([sQuery(id+"F33.wireOp",EDGE,"E182")])]});
            var sketch = newSketch(context, id + "F35", { "sketchPlane" : qUnion([Q0])});
            skCircle(sketch, "E183", {"center": v(-76.8, 0) * mm, "radius": 2 * mm});
            skLineSegment(sketch, "E184", {"start": v(-76.8, 0) * mm, "end": v(-75.2, 0) * mm});
            skLineSegment(sketch, "E185", {"start": v(-75.2, 0) * mm, "end": v(-75.2, 1.2) * mm});
            skLineSegment(sketch, "E186.MirrorCS", {"start": v(-75.2, 0) * mm, "end": v(-75.2, -1.2) * mm});
            skLineSegment(sketch, "E187", {"start": v(-76.8, 0) * mm, "end": v(-76.8, 0.42) * mm});
            skLineSegment(sketch, "E188.MirrorCS", {"start": v(-78.4, 0) * mm, "end": v(-78.4, 1.2) * mm});
            skLineSegment(sketch, "E189.MirrorCS", {"start": v(-78.4, 0) * mm, "end": v(-78.4, -1.2) * mm});
            skSolve(sketch);
        }
        {
            var Q0;
            Q0=makeQuery(id+"F35.imprint","IMPRINT",FACE,{"disambiguationData":[TD([[makeQuery(id+"F35.imprint","IMPRINT",EDGE,{"derivedFrom":makeQuery(id+"F34.opRevolve","SWEPT_EDGE",EDGE,{"disambiguationData":[OSD([sQuery(id+"F33.wireOp",EDGE,"E181"),sQuery(id+"F33.wireOp",EDGE,"E182")])]})}),1.0]])]});
            var Q1;
            {var subQ1=sQuery(id+"F35.wireOp",EDGE,"E185");Q1=makeQuery(id+"F35.imprint","IMPRINT",FACE,{"disambiguationData":[TD([[makeQuery(id+"F35.imprint","IMPRINT",EDGE,{"derivedFrom":subQ1}),1.0]])]});}
            extrude(context, id + "F36", {"entities" : qUnion([Q0, Q1]), "operationType" : NewBodyOperationType.ADD, "depth" : 1.5 * mm});
        }
        {
            var Q0;
            Q0=qCreatedBy(makeId("Front.planeOp"),FACE);
            var sketch = newSketch(context, id + "F37", { "sketchPlane" : qUnion([Q0])});
            skCircle(sketch, "E190", {"center": v(-73.52, 62.26) * mm, "radius": 2.5 * mm});
            skCircle(sketch, "E191", {"center": v(-73.52, 62.26) * mm, "radius": 1 * mm});
            skSolve(sketch);
        }
        {
            var Q0;
            Q0 = qSketchRegion(id + "F37", true);
            extrude(context, id + "F38", {"entities" : qUnion([Q0]), "depth" : 5 * mm});
        }
        {
            var Q0;
            Q0=qCreatedBy(makeId("Front.planeOp"),FACE);
            var sketch = newSketch(context, id + "F39", { "sketchPlane" : qUnion([Q0])});
            skLineSegment(sketch, "E192", {"start": v(32.48, 83.12) * mm, "end": v(32.48, 84.62) * mm});
            skLineSegment(sketch, "E193", {"start": v(32.48, 84.62) * mm, "end": v(60.23, 84.62) * mm});
            skPoint(sketch, "E194.endSnap0", {"position": v(46.36, 84.62) * mm});
            skLineSegment(sketch, "E195", {"start": v(32.48, 83.12) * mm, "end": v(60.23, 83.12) * mm});
            skLineSegment(sketch, "E196", {"start": v(60.23, 83.12) * mm, "end": v(60.23, 87.12) * mm});
            skLineSegment(sketch, "E197", {"start": v(60.23, 87.12) * mm, "end": v(68.23, 87.12) * mm});
            skLineSegment(sketch, "E198", {"start": v(68.23, 87.12) * mm, "end": v(68.23, 83.12) * mm});
            skLineSegment(sketch, "E199", {"start": v(68.23, 83.12) * mm, "end": v(68.23, 84.62) * mm});
            skLineSegment(sketch, "E200", {"start": v(68.23, 84.62) * mm, "end": v(102.48, 84.62) * mm});
            skLineSegment(sketch, "E201", {"start": v(102.48, 84.62) * mm, "end": v(102.48, 83.12) * mm});
            skLineSegment(sketch, "E202", {"start": v(102.48, 83.12) * mm, "end": v(68.23, 83.12) * mm});
            skLineSegment(sketch, "E203", {"start": v(60.23, 83.12) * mm, "end": v(68.23, 83.12) * mm});
            skSolve(sketch);
        }
        {
            var Q0;
            Q0 = qSketchRegion(id + "F39", true);
            var Q1;
            Q1=sQuery(id+"F39.wireOp",EDGE,"E195");
            revolve(context, id + "F40", {"entities" : qUnion([Q0]), "axis" : qUnion([Q1]), "revolveType" : RevolveType.FULL});
        }
        {
            var Q0;
            Q0=makeQuery(id+"F40.opRevolve","SWEPT_FACE",FACE,{"disambiguationData":[OSD([sQuery(id+"F39.wireOp",EDGE,"E198")])]});
            var sketch = newSketch(context, id + "F41", { "sketchPlane" : qUnion([Q0])});
            skCircle(sketch, "E204", {"center": v(0, 83.12) * mm, "radius": 4 * mm});
            skLineSegment(sketch, "E205", {"start": v(0, 83.12) * mm, "end": v(0, 108.12) * mm});
            skLineSegment(sketch, "E206", {"start": v(0, 108.12) * mm, "end": v(-1, 108.12) * mm});
            skLineSegment(sketch, "E207", {"start": v(-1, 108.12) * mm, "end": v(-3.97, 83.6) * mm});
            skLineSegment(sketch, "E208.MirrorCS", {"start": v(1, 108.12) * mm, "end": v(3.97, 83.6) * mm});
            skLineSegment(sketch, "E209.MirrorCS", {"start": v(0, 108.12) * mm, "end": v(1, 108.12) * mm});
            skSolve(sketch);
        }
        {
            var Q0;
            Q0 = qSketchRegion(id + "F41", true);
            extrude(context, id + "F42", {"entities" : qUnion([Q0]), "operationType" : NewBodyOperationType.ADD, "oppositeDirection" : true, "depth" : 1.5 * mm});
        }
        {
            var Q0;
            Q0=makeQuery(id+"F42.boolean.opBoolean","MERGE",FACE,{"derivedFrom":[makeQuery(id+"F40.opRevolve","SWEPT_FACE",FACE,{"disambiguationData":[OSD([sQuery(id+"F39.wireOp",EDGE,"E198")])]}),makeQuery(id+"F42.opExtrude","CAP_FACE",FACE,{"disambiguationData":[OSD([sQuery(id+"F41.wireOp",EDGE,"E204"),sQuery(id+"F41.wireOp",EDGE,"E206"),sQuery(id+"F41.wireOp",EDGE,"E207"),sQuery(id+"F41.wireOp",EDGE,"E208.MirrorCS"),sQuery(id+"F41.wireOp",EDGE,"E209.MirrorCS")])],"isStart":true})]});
            cPlane(context, id + "F43", {"entities" : qUnion([Q0]), "cplaneType" : CPlaneType.OFFSET, "offset" : (1.5 / 2) * mm, "oppositeDirection" : true, "width" : 150 * mm, "height" : 150 * mm});
        }
        {
            var Q0;
            Q0=qCreatedBy(id+"F43.planeOp",FACE);
            var sketch = newSketch(context, id + "F44", { "sketchPlane" : qUnion([Q0])});
            skLineSegment(sketch, "E210", {"start": v(0, 108.04) * mm, "end": v(0, 123.04) * mm});
            skArc(sketch, "E211", {"start": v(0, 120.04) * mm, "mid": v(3, 123.04) * mm, "end": v(0, 126.04) * mm});
            skArc(sketch, "E212", {"start": v(2, 108.04) * mm, "mid": v(1.41, 109.45) * mm, "end": v(0, 110.04) * mm});
            skArc(sketch, "E213", {"start": v(2.6, 121.55) * mm, "mid": v(1.36, 114.84) * mm, "end": v(2, 108.04) * mm});
            skLineSegment(sketch, "E214", {"start": v(0, 120.04) * mm, "end": v(0, 126.04) * mm});
            skLineSegment(sketch, "E215", {"start": v(0, 108.04) * mm, "end": v(0, 106.04) * mm});
            skLineSegment(sketch, "E216", {"start": v(0, 108.04) * mm, "end": v(2, 108.04) * mm});
            skSolve(sketch);
        }
        {
            var Q0;
            Q0 = qSketchRegion(id + "F44", true);
            var Q1;
            Q1=sQuery(id+"F44.wireOp",EDGE,"E210");
            revolve(context, id + "F45", {"operationType" : NewBodyOperationType.ADD, "entities" : qUnion([Q0]), "axis" : qUnion([Q1]), "revolveType" : RevolveType.FULL});
        }
        {
            var Q0;
            Q0=makeQuery(id+"F45.boolean.opBoolean","INTERSECT",EDGE,{"derivedFrom":[makeQuery(id+"F42.boolean.opBoolean","MERGE",FACE,{"derivedFrom":[makeQuery(id+"F40.opRevolve","SWEPT_FACE",FACE,{"disambiguationData":[OSD([sQuery(id+"F39.wireOp",EDGE,"E198")])]}),makeQuery(id+"F42.opExtrude","CAP_FACE",FACE,{"disambiguationData":[OSD([sQuery(id+"F41.wireOp",EDGE,"E204"),sQuery(id+"F41.wireOp",EDGE,"E206"),sQuery(id+"F41.wireOp",EDGE,"E207"),sQuery(id+"F41.wireOp",EDGE,"E208.MirrorCS"),sQuery(id+"F41.wireOp",EDGE,"E209.MirrorCS")])],"isStart":true})]}),makeQuery(id+"F45.opRevolve","SWEPT_FACE",FACE,{"disambiguationData":[OSD([sQuery(id+"F44.wireOp",EDGE,"E216")])]})]});
            var Q1;
            Q1=makeQuery(id+"F45.boolean.opBoolean","INTERSECT",EDGE,{"derivedFrom":[makeQuery(id+"F42.opExtrude","SWEPT_FACE",FACE,{"disambiguationData":[OSD([sQuery(id+"F41.wireOp",EDGE,"E208.MirrorCS")])]}),makeQuery(id+"F45.opRevolve","SWEPT_FACE",FACE,{"disambiguationData":[OSD([sQuery(id+"F44.wireOp",EDGE,"E216")])]})]});
            var Q2;
            Q2=makeQuery(id+"F45.boolean.opBoolean","INTERSECT",EDGE,{"derivedFrom":[makeQuery(id+"F42.opExtrude","CAP_FACE",FACE,{"disambiguationData":[OSD([sQuery(id+"F41.wireOp",EDGE,"E204"),sQuery(id+"F41.wireOp",EDGE,"E206"),sQuery(id+"F41.wireOp",EDGE,"E207"),sQuery(id+"F41.wireOp",EDGE,"E208.MirrorCS"),sQuery(id+"F41.wireOp",EDGE,"E209.MirrorCS")])],"isStart":false}),makeQuery(id+"F45.opRevolve","SWEPT_FACE",FACE,{"disambiguationData":[OSD([sQuery(id+"F44.wireOp",EDGE,"E216")])]})]});
            var Q3;
            Q3=makeQuery(id+"F45.boolean.opBoolean","INTERSECT",EDGE,{"derivedFrom":[makeQuery(id+"F42.opExtrude","SWEPT_FACE",FACE,{"disambiguationData":[OSD([sQuery(id+"F41.wireOp",EDGE,"E207")])]}),makeQuery(id+"F45.opRevolve","SWEPT_FACE",FACE,{"disambiguationData":[OSD([sQuery(id+"F44.wireOp",EDGE,"E216")])]})]});
            fillet(context, id + "F46", {"entities" : qUnion([Q0, Q1, Q2, Q3]), "radius" : .5 * mm, "tangentPropagation" : true, "allowEdgeOverflow" : false});
        }
        {
            var Q0;
            Q0=qCreatedBy(makeId("Top.planeOp"),FACE);
            cPlane(context, id + "F47", {"entities" : qUnion([Q0]), "cplaneType" : CPlaneType.OFFSET, "offset" : 115 * mm, "width" : 150 * mm, "height" : 150 * mm});
        }
        {
            var Q0;
            Q0=qCreatedBy(id+"F47.planeOp",FACE);
            var sketch = newSketch(context, id + "F48", { "sketchPlane" : qUnion([Q0])});
            skLineSegment(sketch, "E217", {"start": v(32.47, 0) * mm, "end": v(34.47, 0) * mm});
            skLineSegment(sketch, "E218", {"start": v(34.47, 0) * mm, "end": v(34.47, 1.5) * mm});
            skLineSegment(sketch, "E219", {"start": v(34.47, 1.5) * mm, "end": v(39.47, 1.5) * mm});
            skLineSegment(sketch, "E220", {"start": v(39.47, 1.5) * mm, "end": v(39.47, 1.25) * mm});
            skLineSegment(sketch, "E221", {"start": v(39.47, 1.25) * mm, "end": v(34.47, 1.25) * mm});
            skSolve(sketch);
        }
        {
            var Q0;
            Q0 = qSketchRegion(id + "F48", true);
            extrude(context, id + "F49", {"entities" : qUnion([Q0]), "operationType" : NewBodyOperationType.REMOVE, "oppositeDirection" : true, "depth" : 100 * mm});
        }
        {
            var Q0;
            Q0=makeQuery(id+"F40.opRevolve","SWEPT_FACE",FACE,{"disambiguationData":[OSD([sQuery(id+"F39.wireOp",EDGE,"E192")])]});
            var sketch = newSketch(context, id + "F50", { "sketchPlane" : qUnion([Q0])});
            skSolve(sketch);
        }
        {
            var Q0;
            Q0 = qSketchRegion(id + "F50", true);
            var Q1;
            Q1=makeQuery(id+"F50.imprint","IMPRINT",FACE,{"disambiguationData":[TD([[makeQuery(id+"F50.imprint","IMPRINT",EDGE,{"derivedFrom":makeQuery(id+"F40.opRevolve","SWEPT_EDGE",EDGE,{"disambiguationData":[OSD([sQuery(id+"F39.wireOp",EDGE,"E192"),sQuery(id+"F39.wireOp",EDGE,"E193")])]})}),1.0]])]});
            extrude(context, id + "F51", {"entities" : qUnion([Q0, Q1]), "operationType" : NewBodyOperationType.ADD, "depth" : 2 * mm});
        }
    });
